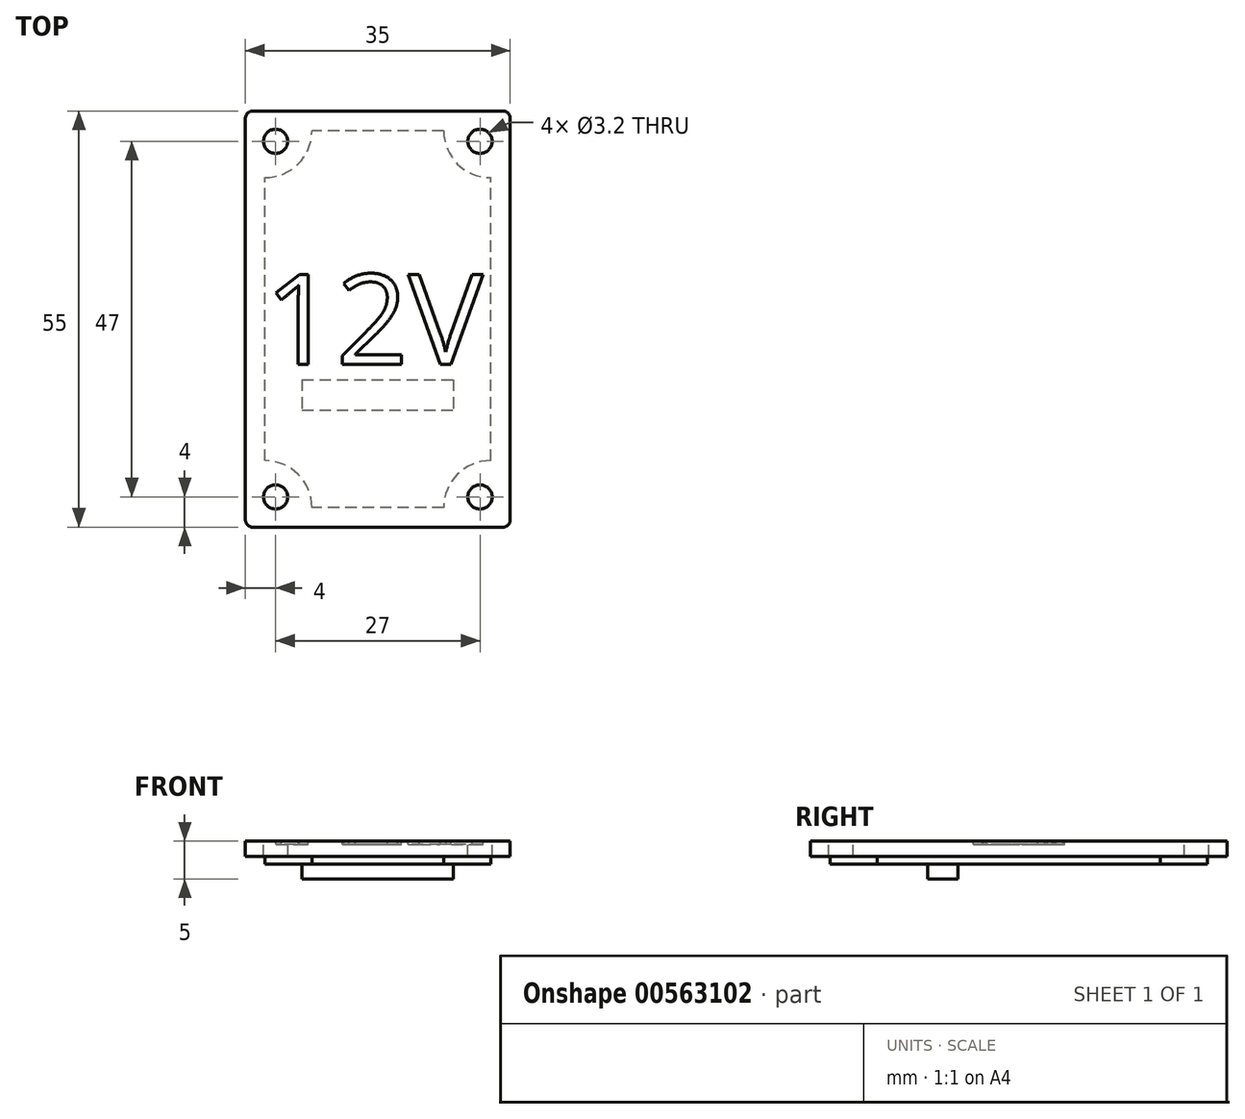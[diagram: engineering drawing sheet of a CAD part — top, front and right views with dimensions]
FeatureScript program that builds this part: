
annotation { "Feature Type Name" : "Feature", "Feature Type Description" : "" }
export const myFeature = defineFeature(function(context is Context, id is Id, definition is map)
    precondition{}
    {
        {
            var Q0;
            Q0=qCreatedBy(makeId("Top.planeOp"),FACE);
            var sketch = newSketch(context, id + "F0", { "sketchPlane" : qUnion([Q0])});
            skLineSegment(sketch, "E0.bottom", {"start": v(8.7, -24.9) * mm, "end": v(-8.7, -24.9) * mm});
            skLineSegment(sketch, "E0.top", {"start": v(8.7, 24.9) * mm, "end": v(-8.7, 24.9) * mm});
            skLineSegment(sketch, "E0.left", {"start": v(14.9, -18.7) * mm, "end": v(14.9, 18.7) * mm});
            skLineSegment(sketch, "E0.right", {"start": v(-14.9, -18.7) * mm, "end": v(-14.9, 18.7) * mm});
            skPoint(sketch, "E0.middle", {"position": v(0, 0) * mm});
            skLineSegment(sketch, "E1.bottom", {"start": v(-17.5, -27.5) * mm, "end": v(17.5, -27.5) * mm});
            skLineSegment(sketch, "E1.top", {"start": v(-17.5, 27.5) * mm, "end": v(17.5, 27.5) * mm});
            skLineSegment(sketch, "E1.left", {"start": v(-17.5, -27.5) * mm, "end": v(-17.5, 27.5) * mm});
            skLineSegment(sketch, "E1.right", {"start": v(17.5, -27.5) * mm, "end": v(17.5, 27.5) * mm});
            skArc(sketch, "E2", {"start": v(8.7, 24.9) * mm, "mid": v(10.52, 20.52) * mm, "end": v(14.9, 18.7) * mm});
            skArc(sketch, "E3", {"start": v(-8.7, 24.9) * mm, "mid": v(-10.52, 20.52) * mm, "end": v(-14.9, 18.7) * mm});
            skArc(sketch, "E4", {"start": v(-14.9, -18.7) * mm, "mid": v(-10.52, -20.52) * mm, "end": v(-8.7, -24.9) * mm});
            skArc(sketch, "E5", {"start": v(14.9, -18.7) * mm, "mid": v(10.52, -20.52) * mm, "end": v(8.7, -24.9) * mm});
            skLineSegment(sketch, "E6", {"start": v(-17.5, 27.5) * mm, "end": v(-13.5, 27.5) * mm, "construction": true});
            skLineSegment(sketch, "E7", {"start": v(-13.5, 27.5) * mm, "end": v(-13.5, 23.5) * mm, "construction": true});
            skCircle(sketch, "E8", {"center": v(-13.5, 23.5) * mm, "radius": 1.6 * mm});
            skCircle(sketch, "E9.MirrorC", {"center": v(13.5, 23.5) * mm, "radius": 1.6 * mm});
            skCircle(sketch, "E10.MirrorC", {"center": v(-13.5, -23.5) * mm, "radius": 1.6 * mm});
            skCircle(sketch, "E11.MirrorC", {"center": v(13.5, -23.5) * mm, "radius": 1.6 * mm});
            skSolve(sketch);
        }
        {
            var Q0;
            Q0=makeQuery(id+"F0.imprint","IMPRINT",FACE,{"disambiguationData":[TD([[makeQuery(id+"F0.imprint","IMPRINT",EDGE,{"derivedFrom":sQuery(id+"F0.wireOp",EDGE,"E0.bottom")}),1.0]])]});
            extrude(context, id + "F1", {"entities" : qUnion([Q0]), "oppositeDirection" : true, "depth" : 2 * mm, "offsetDistance" : 25 * mm});
        }
        {
            var Q0;
            Q0=makeQuery(id+"F0.imprint","IMPRINT",FACE,{"disambiguationData":[TD([[makeQuery(id+"F0.imprint","IMPRINT",EDGE,{"derivedFrom":sQuery(id+"F0.wireOp",EDGE,"E0.bottom")}),-1.0]])]});
            extrude(context, id + "F2", {"entities" : qUnion([Q0]), "operationType" : NewBodyOperationType.ADD, "oppositeDirection" : true, "depth" : 3 * mm, "offsetDistance" : 25 * mm});
        }
        {
            var Q0;
            Q0=makeQuery(id+"F1.opExtrude","SWEPT_EDGE",EDGE,{"disambiguationData":[OSD([sQuery(id+"F0.wireOp",EDGE,"E1.top"),sQuery(id+"F0.wireOp",EDGE,"E1.right")])]});
            var Q1;
            Q1=makeQuery(id+"F1.opExtrude","SWEPT_EDGE",EDGE,{"disambiguationData":[OSD([sQuery(id+"F0.wireOp",EDGE,"E1.top"),sQuery(id+"F0.wireOp",EDGE,"E1.left")])]});
            var Q2;
            Q2=makeQuery(id+"F1.opExtrude","SWEPT_EDGE",EDGE,{"disambiguationData":[OSD([sQuery(id+"F0.wireOp",EDGE,"E1.bottom"),sQuery(id+"F0.wireOp",EDGE,"E1.right")])]});
            var Q3;
            Q3=makeQuery(id+"F1.opExtrude","SWEPT_EDGE",EDGE,{"disambiguationData":[OSD([sQuery(id+"F0.wireOp",EDGE,"E1.bottom"),sQuery(id+"F0.wireOp",EDGE,"E1.left")])]});
            fillet(context, id + "F3", {"entities" : qUnion([Q0, Q1, Q2, Q3]), "radius" : 1 * mm, "tangentPropagation" : true, "allowEdgeOverflow" : false});
        }
        {
            var Q0;
            Q0=qCreatedBy(makeId("Top.planeOp"),FACE);
            var sketch = newSketch(context, id + "F4", { "sketchPlane" : qUnion([Q0])});
            skLineSegment(sketch, "E12.bottom", {"start": v(-10, -8) * mm, "end": v(10, -8) * mm, "construction": true});
            skLineSegment(sketch, "E12.top", {"start": v(-10, 8) * mm, "end": v(10, 8) * mm, "construction": true});
            skLineSegment(sketch, "E12.left", {"start": v(-10, -8) * mm, "end": v(-10, 8) * mm, "construction": true});
            skLineSegment(sketch, "E12.right", {"start": v(10, -8) * mm, "end": v(10, 8) * mm, "construction": true});
            skPoint(sketch, "E12.middle", {"position": v(0, 0) * mm});
            skLineSegment(sketch, "E13.bottom", {"start": v(-10, -8) * mm, "end": v(10, -8) * mm});
            skLineSegment(sketch, "E13.top", {"start": v(-10, -12) * mm, "end": v(10, -12) * mm});
            skLineSegment(sketch, "E13.left", {"start": v(-10, -8) * mm, "end": v(-10, -12) * mm});
            skLineSegment(sketch, "E13.right", {"start": v(10, -8) * mm, "end": v(10, -12) * mm});
            skSolve(sketch);
        }
        {
            var Q0;
            Q0 = qSketchRegion(id + "F4", true);
            extrude(context, id + "F5", {"entities" : qUnion([Q0]), "operationType" : NewBodyOperationType.ADD, "oppositeDirection" : true, "depth" : 5 * mm, "offsetDistance" : 25 * mm});
        }
        {
            var Q0;
            Q0=qCreatedBy(makeId("Top.planeOp"),FACE);
            var sketch = newSketch(context, id + "F6", { "sketchPlane" : qUnion([Q0])});
            skText(sketch, "E14", { "text": "12V\n", "fontName": "OpenSans-Regular.ttf"});
            const initialGuessF6  = {"E14": [-0.015, -0.00598, 1, 0, 0.01198]};
            skSetInitialGuess(sketch, initialGuessF6);
            skSolve(sketch);
        }
        {
            var Q0;
            Q0 = qSketchRegion(id + "F6", true);
            extrude(context, id + "F7", {"entities" : qUnion([Q0]), "operationType" : NewBodyOperationType.REMOVE, "oppositeDirection" : true, "depth" : .4 * mm, "offsetDistance" : 25 * mm, "hasSecondDirection" : true, "secondDirectionOppositeDirection" : false, "secondDirectionDepth" : 25 * mm});
        }
    });
